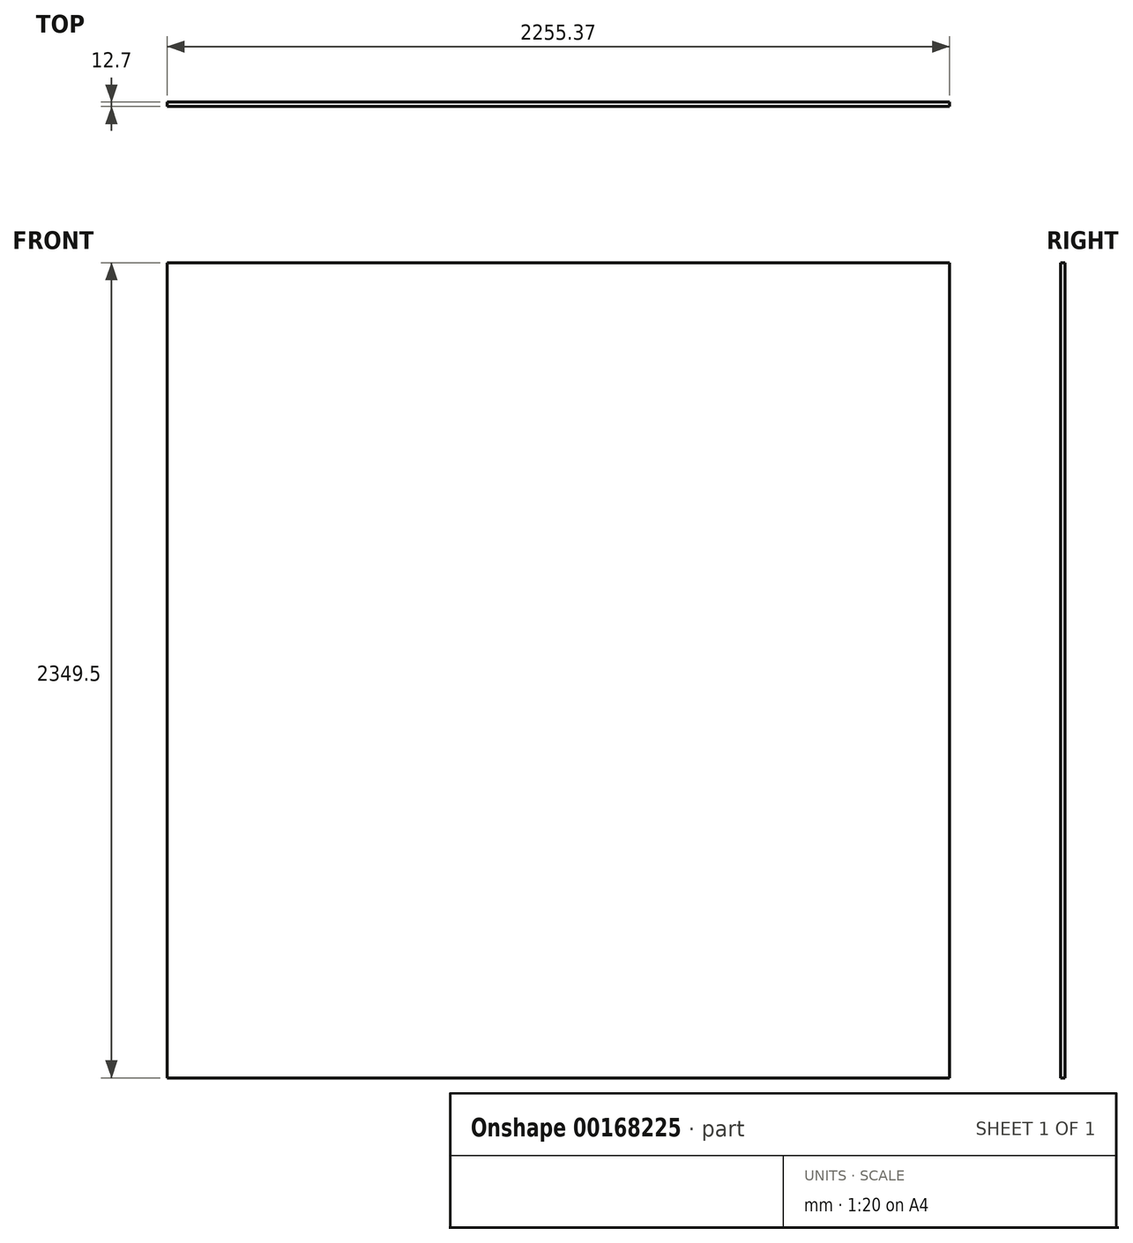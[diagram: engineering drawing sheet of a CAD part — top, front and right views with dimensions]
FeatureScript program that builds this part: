
annotation { "Feature Type Name" : "Feature", "Feature Type Description" : "" }
export const myFeature = defineFeature(function(context is Context, id is Id, definition is map)
    precondition{}
    {
        {
            var Q0;
            Q0=qCreatedBy(makeId("Front.planeOp"),FACE);
            var sketch = newSketch(context, id + "F0", { "sketchPlane" : qUnion([Q0])});
            skLineSegment(sketch, "E0.bottom", {"start": v(-1126.41, 1172.5) * mm, "end": v(1128.96, 1172.5) * mm});
            skLineSegment(sketch, "E0.top", {"start": v(-1126.41, -1177) * mm, "end": v(1128.96, -1177) * mm});
            skLineSegment(sketch, "E0.left", {"start": v(-1126.41, 1172.5) * mm, "end": v(-1126.41, -1177) * mm});
            skLineSegment(sketch, "E0.right", {"start": v(1128.96, 1172.5) * mm, "end": v(1128.96, -1177) * mm});
            skSolve(sketch);
        }
        {
            var Q0;
            Q0=makeQuery(id+"F0.imprint","IMPRINT",FACE,{"disambiguationData":[TD([[makeQuery(id+"F0.imprint","IMPRINT",EDGE,{"derivedFrom":sQuery(id+"F0.wireOp",EDGE,"E0.bottom")}),-1.0]])]});
            extrude(context, id + "F1", {"entities" : qUnion([Q0]), "depth" : 12.7 * mm});
        }
    });
